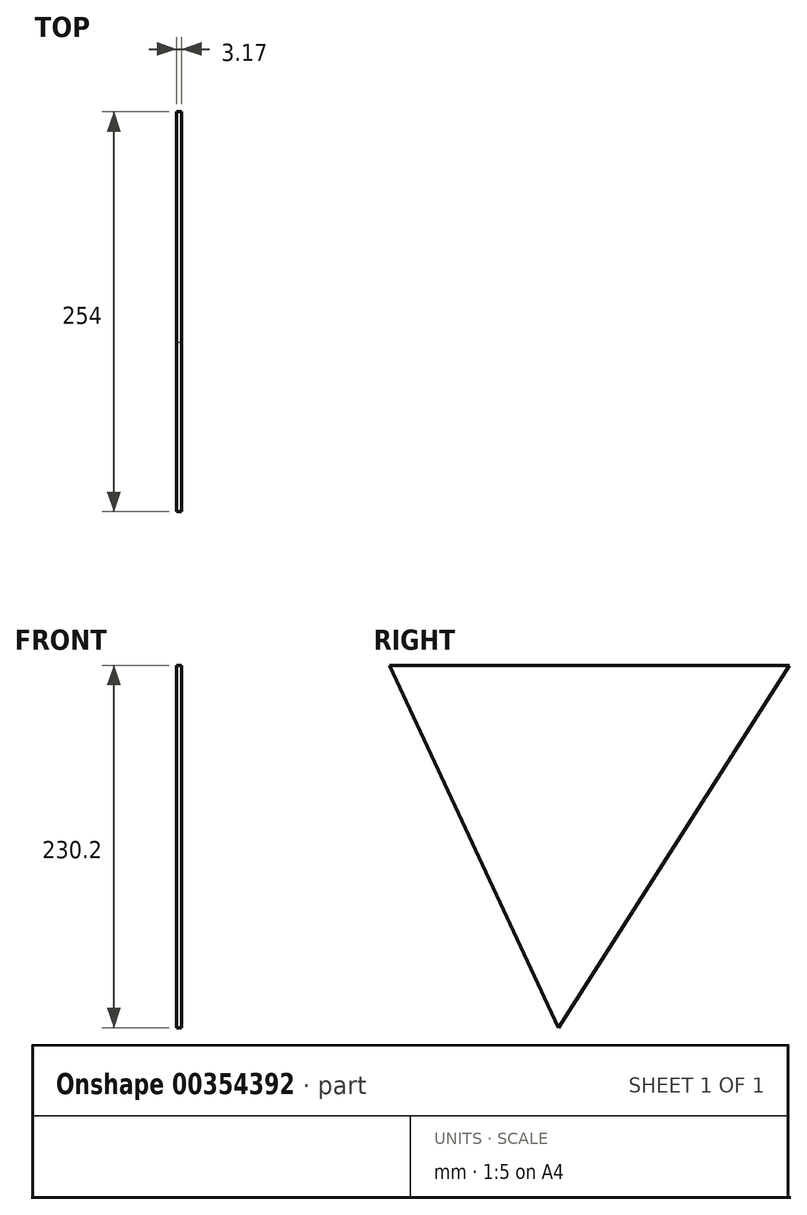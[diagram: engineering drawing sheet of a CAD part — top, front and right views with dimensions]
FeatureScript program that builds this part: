
annotation { "Feature Type Name" : "Feature", "Feature Type Description" : "" }
export const myFeature = defineFeature(function(context is Context, id is Id, definition is map)
    precondition{}
    {
        {
            var Q0;
            Q0=qCreatedBy(makeId("Right.planeOp"),FACE);
            var sketch = newSketch(context, id + "F0", { "sketchPlane" : qUnion([Q0])});
            skLineSegment(sketch, "E0.bottom", {"start": v(127, 127) * mm, "end": v(-127, 127) * mm});
            skPoint(sketch, "E0.middle", {"position": v(0, 0) * mm});
            skPoint(sketch, "E0.top.start.orphan", {"position": v(127, -127) * mm});
            skLineSegment(sketch, "E1", {"start": v(127, 127) * mm, "end": v(127, -127) * mm});
            skLineSegment(sketch, "E2", {"start": v(-127, 127) * mm, "end": v(-19.65, -103.2) * mm});
            skPoint(sketch, "E3.orphan", {"position": v(-127, -127) * mm});
            skLineSegment(sketch, "E4", {"start": v(127, 127) * mm, "end": v(-19.65, -103.2) * mm});
            skSolve(sketch);
        }
        {
            var Q0;
            Q0 = qSketchRegion(id + "F0", true);
            extrude(context, id + "F1", {"entities" : qUnion([Q0]), "depth" : 3.17 * mm});
        }
    });
